FCSTD DOCUMENT  (FreeCAD 0.16R6706 (Git))
Label: femur
License: All rights reserved
LicenseURL: http://en.wikipedia.org/wiki/All_rights_reserved
objects: Sketcher::SketchObject×4
note: 4 computed .brp shape members not serialized (recipe doc carries the construction recipe); baked Part::Feature solids carry a one-line shape summary decoded from their .brp

FEATURE [Sketcher::SketchObject] Sketch003  label="femur_down"
  sketch-geometry (37):
    g0: LineSegment [constr] StartX=-7.72642 StartY=27.2442 StartZ=0 EndX=52.2736 EndY=27.2442 EndZ=0
    g1: GeomPoint [constr] X=-7.72642 Y=27.2442 Z=0
    g2: GeomPoint [constr] X=52.2736 Y=27.2442 Z=0
    g3: GeomPoint [constr] X=22.2736 Y=27.2442 Z=0
    g4: LineSegment [constr] StartX=22.2736 StartY=32.7442 StartZ=0 EndX=22.2736 EndY=21.7442 EndZ=0
    g5: LineSegment [constr] StartX=-7.72642 StartY=32.7442 StartZ=0 EndX=52.2736 EndY=32.7442 EndZ=0
    g6: LineSegment [constr] StartX=-7.72642 StartY=21.7442 StartZ=0 EndX=52.2736 EndY=21.7442 EndZ=0
    g7: Circle CenterX=52.2736 CenterY=27.2442 CenterZ=0 NormalX=0 NormalY=0 NormalZ=1 Radius=1.5
    g8: Circle CenterX=-7.72642 CenterY=27.2442 CenterZ=0 NormalX=0 NormalY=0 NormalZ=1 Radius=1.5
    g9: ArcOfCircle CenterX=52.2736 CenterY=27.2442 CenterZ=0 NormalX=0 NormalY=0 NormalZ=1 Radius=5.5 StartAngle=4.71239 EndAngle=7.85398
    g10: ArcOfCircle CenterX=-7.72642 CenterY=27.2442 CenterZ=0 NormalX=0 NormalY=0 NormalZ=1 Radius=5.5 StartAngle=1.5708 EndAngle=4.71239
    g11: LineSegment StartX=52.2736 StartY=32.7442 StartZ=0 EndX=32.0066 EndY=32.7442 EndZ=0
    g12: LineSegment [constr] StartX=29.0066 StartY=32.7442 StartZ=0 EndX=29.0066 EndY=24.7442 EndZ=0
    g13: LineSegment StartX=32.0066 StartY=21.7442 StartZ=0 EndX=32.0066 EndY=24.7442 EndZ=0
    g14: LineSegment StartX=29.0066 StartY=24.7442 StartZ=0 EndX=32.0066 EndY=24.7442 EndZ=0
    g15: LineSegment StartX=52.2736 StartY=21.7442 StartZ=0 EndX=32.0066 EndY=21.7442 EndZ=0
    g16: GeomPoint [constr] X=29.0066 Y=32.7442 Z=0
    g17: LineSegment StartX=29.0066 StartY=29.7442 StartZ=0 EndX=32.0066 EndY=29.7442 EndZ=0
    g18: LineSegment StartX=-7.72642 StartY=21.7442 StartZ=0 EndX=7.29856 EndY=21.7442 EndZ=0
    g19: LineSegment StartX=29.0066 StartY=24.7442 StartZ=0 EndX=29.0066 EndY=21.7442 EndZ=0
    g20: LineSegment [constr] StartX=18.6653 StartY=32.7442 StartZ=0 EndX=10.9612 EndY=21.7442 EndZ=0
    g21: LineSegment StartX=16.9443 StartY=30.287 StartZ=0 EndX=14.487 EndY=32.008 EndZ=0
    g22: LineSegment StartX=14.487 StartY=32.008 StartZ=0 EndX=15.0027 EndY=32.7442 EndZ=0
    g23: LineSegment StartX=-7.72642 StartY=32.7442 StartZ=0 EndX=15.0027 EndY=32.7442 EndZ=0
    g24: LineSegment StartX=10.9612 StartY=21.7442 StartZ=0 EndX=11.4768 EndY=22.4805 EndZ=0
    g25: LineSegment StartX=11.4768 StartY=22.4805 StartZ=0 EndX=9.01956 EndY=24.2015 EndZ=0
    g26: LineSegment StartX=9.01956 StartY=24.2015 StartZ=0 EndX=7.29856 EndY=21.7442 EndZ=0
    g27: LineSegment StartX=29.0066 StartY=21.7442 StartZ=0 EndX=10.9612 EndY=21.7442 EndZ=0
    g28: LineSegment StartX=29.0066 StartY=29.7442 StartZ=0 EndX=29.0066 EndY=32.7442 EndZ=0
    g29: LineSegment StartX=16.9443 StartY=30.287 StartZ=0 EndX=18.6653 EndY=32.7442 EndZ=0
    g30: LineSegment StartX=18.6653 StartY=32.7442 StartZ=0 EndX=29.0066 EndY=32.7442 EndZ=0
    g31: LineSegment [constr] StartX=29.0066 StartY=32.7442 StartZ=0 EndX=32.0066 EndY=32.7442 EndZ=0
    g32: LineSegment [constr] StartX=18.6653 StartY=32.7442 StartZ=0 EndX=16.208 EndY=34.4653 EndZ=0
    g33: LineSegment [constr] StartX=15.0027 StartY=32.7442 StartZ=0 EndX=16.208 EndY=34.4653 EndZ=0
    g34: Circle CenterX=21.7923 CenterY=27.2442 CenterZ=0 NormalX=0 NormalY=0 NormalZ=1 Radius=1.2
    g35: LineSegment [constr] StartX=22.9754 StartY=30.0156 StartZ=0 EndX=20.2417 EndY=23.6124 EndZ=0
    g36: LineSegment StartX=32.0066 StartY=32.7442 StartZ=0 EndX=32.0066 EndY=29.7442 EndZ=0
  constraints (96):
    c: PointOnObject(g1,g0)
    c: PointOnObject(g2,g0)
    c: Symmetric(g1,g2,g3)
    c: Distance(g3,g2) = 30
    c: Vertical(g4)
    c: Symmetric(g4,g4,g3)
    c: Distance(g3,g4) = 5.5
    c: Horizontal(g5)
    c: PointOnObject(g4,g5)
    c: Horizontal(g6)
    c: PointOnObject(g4,g6)
    c: Coincident(g7,g2)
    c: Radius(g7) = 1.5
    c: Coincident(g8,g1)
    c: Radius(g8) = 1.5
    c: Coincident(g9,g2)
    c: Coincident(g9,g6)
    c: Coincident(g5,g9)
    c: Tangent(g9,g5)
    c: Coincident(g10,g1)
    c: Coincident(g10,g6)
    c: Tangent(g6,g10)
    c: Coincident(g5,g10)
    c: Coincident(g11,g5)
    c: Coincident(g0,g2)
    c: Coincident(g0,g1)
    c: PointOnObject(g14,g12)
    c: Distance(g13,g13) = 3
    c: Coincident(g14,g13)
    c: Coincident(g15,g6)
    c: Perpendicular(g14,g12)
    c: Perpendicular(g14,g13)
    c: Distance(g13,g12) = 3
    c: PointOnObject(g17,g12)
    c: Distance(g17,g16) = 3
    c: Distance(g17,g17) = 3
    c: Perpendicular(g12,g17)
    c: PointOnObject(g12,g14)
    c: Coincident(g18,g6)
    c: PointOnObject(g13,g6)
    c: Coincident(g15,g13)
    c: Coincident(g19,g12)
    c: PointOnObject(g19,g6)
    c: Perpendicular(g14,g19)
    c: PointOnObject(g20,g6)
    c: PointOnObject(g21,g20)
    c: Distance(g21,g20) = 3
    c: Distance(g21,g21) = 3
    c: Perpendicular(g20,g21)
    c: Coincident(g22,g21)
    c: PointOnObject(g22,g5)
    c: Perpendicular(g21,g22)
    c: Coincident(g23,g5)
    c: Coincident(g22,g23)
    c: Coincident(g24,g20)
    c: PointOnObject(g24,g20)
    c: Coincident(g25,g24)
    c: Distance(g25,g24) = 3
    c: Coincident(g26,g25)
    c: PointOnObject(g26,g6)
    c: Distance(g26,g25) = 3
    c: Perpendicular(g25,g26)
    c: Perpendicular(g20,g25)
    c: Coincident(g18,g26)
    c: Coincident(g27,g19)
    c: Coincident(g20,g27)
    c: Coincident(g28,g12)
    c: Coincident(g17,g28)
    c: Coincident(g16,g12)
    c: PointOnObject(g12,g5)
    c: PointOnObject(g20,g5)
    c: Coincident(g29,g21)
    c: Coincident(g20,g29)
    c: Coincident(g30,g20)
    c: Coincident(g12,g30)
    c: Distance(g13,g0) = 21
    c: Tangent(g6,g9)
    c: Coincident(g31,g12)
    c: Perpendicular(g31,g12)
    c: Coincident(g32,g20)
    c: Perpendicular(g20,g32)
    c: Coincident(g33,g22)
    c: Parallel(g33,g22)
    c: Coincident(g32,g33)
    c: Distance(g18,g0) = 16
    c: Distance(g32,g0) = 25
    c: Radius(g34) = 1.2
    c: Symmetric(g24,g12,g35)
    c: Symmetric(g21,g17,g35)
    c: PointOnObject(g34,g35)
    c: PointOnObject(g34,g0)
    c: Coincident(g11,g31)
    c: Distance(g12,g11) = 3
    c: Coincident(g36,g11)
    c: Coincident(g17,g36)
    c: Horizontal(g11)
FEATURE [Sketcher::SketchObject] Sketch004  label="femur_up"
  sketch-geometry (51):
    g0: LineSegment [constr] StartX=-8.28939 StartY=9.55012 StartZ=0 EndX=51.7106 EndY=9.55012 EndZ=0
    g1: GeomPoint [constr] X=-8.28939 Y=9.55012 Z=0
    g2: GeomPoint [constr] X=51.7106 Y=9.55012 Z=0
    g3: GeomPoint [constr] X=21.7106 Y=9.55012 Z=0
    g4: LineSegment [constr] StartX=21.7106 StartY=15.0501 StartZ=0 EndX=21.7106 EndY=4.05012 EndZ=0
    g5: LineSegment [constr] StartX=-8.28939 StartY=15.0501 StartZ=0 EndX=51.7106 EndY=15.0501 EndZ=0
    g6: LineSegment [constr] StartX=-8.28939 StartY=4.05012 StartZ=0 EndX=51.7106 EndY=4.05012 EndZ=0
    g7: Circle CenterX=51.7106 CenterY=9.55012 CenterZ=0 NormalX=0 NormalY=0 NormalZ=1 Radius=3.5
    g8: Circle CenterX=-8.28939 CenterY=9.55012 CenterZ=0 NormalX=0 NormalY=0 NormalZ=1 Radius=3.5
    g9: LineSegment StartX=51.7106 StartY=15.0501 StartZ=0 EndX=31.4436 EndY=15.0501 EndZ=0
    g10: LineSegment [constr] StartX=28.4436 StartY=15.0501 StartZ=0 EndX=28.4436 EndY=7.05012 EndZ=0
    g11: LineSegment StartX=31.4436 StartY=4.05012 StartZ=0 EndX=31.4436 EndY=7.05012 EndZ=0
    g12: LineSegment StartX=28.4436 StartY=7.05012 StartZ=0 EndX=31.4436 EndY=7.05012 EndZ=0
    g13: LineSegment StartX=51.7106 StartY=4.05012 StartZ=0 EndX=31.4436 EndY=4.05012 EndZ=0
    g14: GeomPoint [constr] X=28.4436 Y=15.0501 Z=0
    g15: LineSegment StartX=28.4436 StartY=12.0501 StartZ=0 EndX=31.4436 EndY=12.0501 EndZ=0
    g16: LineSegment StartX=-8.28939 StartY=4.05012 StartZ=0 EndX=6.73559 EndY=4.05012 EndZ=0
    g17: LineSegment StartX=28.4436 StartY=7.05012 StartZ=0 EndX=28.4436 EndY=4.05012 EndZ=0
    g18: LineSegment [constr] StartX=18.1023 StartY=15.0501 StartZ=0 EndX=10.3982 EndY=4.05012 EndZ=0
    g19: LineSegment StartX=16.3813 StartY=12.5929 StartZ=0 EndX=13.924 EndY=14.3139 EndZ=0
    g20: LineSegment StartX=13.924 StartY=14.3139 StartZ=0 EndX=14.4397 EndY=15.0501 EndZ=0
    g21: LineSegment StartX=-8.28939 StartY=15.0501 StartZ=0 EndX=14.4397 EndY=15.0501 EndZ=0
    g22: LineSegment StartX=10.3982 StartY=4.05012 StartZ=0 EndX=10.9139 EndY=4.78638 EndZ=0
    g23: LineSegment StartX=10.9139 StartY=4.78638 StartZ=0 EndX=8.45659 EndY=6.50739 EndZ=0
    g24: LineSegment StartX=8.45659 StartY=6.50739 StartZ=0 EndX=6.73559 EndY=4.05012 EndZ=0
    g25: LineSegment StartX=28.4436 StartY=4.05012 StartZ=0 EndX=10.3982 EndY=4.05012 EndZ=0
    g26: LineSegment StartX=28.4436 StartY=12.0501 StartZ=0 EndX=28.4436 EndY=15.0501 EndZ=0
    g27: LineSegment StartX=16.3813 StartY=12.5929 StartZ=0 EndX=18.1023 EndY=15.0501 EndZ=0
    g28: LineSegment StartX=18.1023 StartY=15.0501 StartZ=0 EndX=28.4436 EndY=15.0501 EndZ=0
    g29: LineSegment [constr] StartX=28.4436 StartY=15.0501 StartZ=0 EndX=31.4436 EndY=15.0501 EndZ=0
    g30: LineSegment [constr] StartX=18.1023 StartY=15.0501 StartZ=0 EndX=15.645 EndY=16.7711 EndZ=0
    g31: LineSegment [constr] StartX=14.4397 StartY=15.0501 StartZ=0 EndX=15.645 EndY=16.7711 EndZ=0
    g32: Circle CenterX=21.2293 CenterY=9.55012 CenterZ=0 NormalX=0 NormalY=0 NormalZ=1 Radius=1.5
    g33: LineSegment [constr] StartX=22.4125 StartY=12.3215 StartZ=0 EndX=19.6787 EndY=5.91825 EndZ=0
    g34: LineSegment [constr] StartX=51.7106 StartY=15.0501 StartZ=0 EndX=51.7106 EndY=4.05012 EndZ=0
    g35: LineSegment [constr] StartX=-8.28939 StartY=15.0501 StartZ=0 EndX=-8.28939 EndY=4.05012 EndZ=0
    g36: Circle CenterX=45.2106 CenterY=9.55012 CenterZ=0 NormalX=0 NormalY=0 NormalZ=1 Radius=1.2
    g37: Circle CenterX=-1.78939 CenterY=9.55012 CenterZ=0 NormalX=0 NormalY=0 NormalZ=1 Radius=1.2
    g38: Circle CenterX=58.2106 CenterY=9.55012 CenterZ=0 NormalX=0 NormalY=0 NormalZ=1 Radius=1.2
    g39: Circle CenterX=-14.7894 CenterY=9.55012 CenterZ=0 NormalX=0 NormalY=0 NormalZ=1 Radius=1.2
    g40: ArcOfEllipse CenterX=51.7106 CenterY=9.55012 CenterZ=0 NormalX=0 NormalY=0 NormalZ=1 MajorRadius=10.5 MinorRadius=5.5 AngleXU=0 StartAngle=4.71239 EndAngle=7.85398
    g41: LineSegment [constr] StartX=62.2106 StartY=9.55012 StartZ=0 EndX=41.2106 EndY=9.55012 EndZ=0
    g42: LineSegment [constr] StartX=51.7106 StartY=15.0501 StartZ=0 EndX=51.7106 EndY=4.05012 EndZ=0
    g43: GeomPoint [constr] X=60.6549 Y=9.55012 Z=0
    g44: GeomPoint [constr] X=42.7663 Y=9.55012 Z=0
    g45: ArcOfEllipse CenterX=-8.28939 CenterY=9.55012 CenterZ=0 NormalX=0 NormalY=0 NormalZ=1 MajorRadius=10.5 MinorRadius=5.5 AngleXU=0 StartAngle=1.5708 EndAngle=4.71239
    g46: LineSegment [constr] StartX=2.21061 StartY=9.55012 StartZ=0 EndX=-18.7894 EndY=9.55012 EndZ=0
    g47: LineSegment [constr] StartX=-8.28939 StartY=15.0501 StartZ=0 EndX=-8.28939 EndY=4.05012 EndZ=0
    g48: GeomPoint [constr] X=0.654878 Y=9.55012 Z=0
    g49: GeomPoint [constr] X=-17.2337 Y=9.55012 Z=0
    g50: LineSegment StartX=31.4436 StartY=15.0501 StartZ=0 EndX=31.4436 EndY=12.0501 EndZ=0
  constraints (120):
    c: PointOnObject(g1,g0)
    c: PointOnObject(g2,g0)
    c: Symmetric(g1,g2,g3)
    c: Distance(g3,g2) = 30
    c: Vertical(g4)
    c: Symmetric(g4,g4,g3)
    c: Distance(g3,g4) = 5.5
    c: Horizontal(g5)
    c: PointOnObject(g4,g5)
    c: Horizontal(g6)
    c: PointOnObject(g4,g6)
    c: Coincident(g7,g2)
    c: Radius(g7) = 3.5
    c: Coincident(g8,g1)
    c: Radius(g8) = 3.5
    c: Coincident(g9,g5)
    c: Coincident(g0,g2)
    c: Coincident(g0,g1)
    c: PointOnObject(g12,g10)
    c: Distance(g11,g11) = 3
    c: Coincident(g12,g11)
    c: Coincident(g13,g6)
    c: Perpendicular(g12,g10)
    c: Perpendicular(g12,g11)
    c: Distance(g11,g10) = 3
    c: PointOnObject(g15,g10)
    c: Distance(g15,g14) = 3
    c: Distance(g15,g15) = 3
    c: Perpendicular(g10,g15)
    c: PointOnObject(g10,g12)
    c: Coincident(g16,g6)
    c: PointOnObject(g11,g6)
    c: Coincident(g13,g11)
    c: Coincident(g17,g10)
    c: PointOnObject(g17,g6)
    c: Perpendicular(g12,g17)
    c: PointOnObject(g18,g6)
    c: PointOnObject(g19,g18)
    c: Distance(g19,g18) = 3
    c: Distance(g19,g19) = 3
    c: Perpendicular(g18,g19)
    c: Coincident(g20,g19)
    c: PointOnObject(g20,g5)
    c: Perpendicular(g19,g20)
    c: Coincident(g21,g5)
    c: Coincident(g20,g21)
    c: Coincident(g22,g18)
    c: PointOnObject(g22,g18)
    c: Coincident(g23,g22)
    c: Distance(g23,g22) = 3
    c: Coincident(g24,g23)
    c: PointOnObject(g24,g6)
    c: Distance(g24,g23) = 3
    c: Perpendicular(g23,g24)
    c: Perpendicular(g18,g23)
    c: Coincident(g16,g24)
    c: Coincident(g25,g17)
    c: Coincident(g18,g25)
    c: Coincident(g26,g10)
    c: Coincident(g15,g26)
    c: Coincident(g14,g10)
    c: PointOnObject(g10,g5)
    c: PointOnObject(g18,g5)
    c: Coincident(g27,g19)
    c: Coincident(g18,g27)
    c: Coincident(g28,g18)
    c: Coincident(g10,g28)
    c: Distance(g11,g0) = 21
    c: Coincident(g29,g10)
    c: Perpendicular(g29,g10)
    c: Coincident(g30,g18)
    c: Perpendicular(g18,g30)
    c: Coincident(g31,g20)
    c: Parallel(g31,g20)
    c: Coincident(g30,g31)
    c: Distance(g16,g0) = 16
    c: Distance(g30,g0) = 25
    c: Radius(g32) = 1.5
    c: Symmetric(g22,g10,g33)
    c: Symmetric(g19,g15,g33)
    c: PointOnObject(g32,g33)
    c: Coincident(g34,g5)
    c: Coincident(g34,g6)
    c: Vertical(g34)
    c: Coincident(g35,g5)
    c: Coincident(g35,g6)
    c: Vertical(g35)
    c: PointOnObject(g0,g34)
    c: Distance(g0,g6) = 5.5
    c: PointOnObject(g0,g35)
    c: PointOnObject(g36,g0)
    c: Radius(g36) = 1.2
    c: Distance(g0,g36) = 6.5
    c: PointOnObject(g37,g0)
    c: Radius(g37) = 1.2
    c: Distance(g0,g37) = 6.5
    c: Radius(g38) = 1.2
    c: PointOnObject(g38,g0)
    c: Distance(g0,g38) = 6.5
    c: Radius(g39) = 1.2
    c: PointOnObject(g39,g0)
    c: Distance(g39,g0) = 6.5
    c: InternalAlignment(g41-g44 -> g40) x4
    c: Coincident(g40,g0)
    c: Coincident(g5,g42)
    c: PointOnObject(g40,g34)
    c: PointOnObject(g40,g34)
    c: InternalAlignment(g46-g49 -> g45) x4
    c: Coincident(g45,g0)
    c: Coincident(g6,g47)
    c: PointOnObject(g45,g35)
    c: PointOnObject(g45,g35)
    c: Distance(g38,g41) = 4
    c: Distance(g46,g39) = 4
    c: PointOnObject(g32,g0)
    c: Coincident(g9,g29)
    c: Coincident(g50,g9)
    c: Coincident(g50,g15)
    c: Perpendicular(g50,g15)
    c: Horizontal(g9)
FEATURE [Sketcher::SketchObject] Sketch005  label="femur_joint_tibia"
  sketch-geometry (16):
    g0: LineSegment [constr] StartX=4.47065 StartY=61.2395 StartZ=0 EndX=33.9706 EndY=61.2395 EndZ=0
    g1: LineSegment [constr] StartX=33.9706 StartY=61.2395 StartZ=0 EndX=33.9706 EndY=45.7095 EndZ=0
    g2: LineSegment [constr] StartX=33.9706 StartY=45.7095 StartZ=0 EndX=4.47065 EndY=45.7095 EndZ=0
    g3: LineSegment [constr] StartX=4.47065 StartY=45.7095 StartZ=0 EndX=4.47065 EndY=61.2395 EndZ=0
    g4: LineSegment StartX=1.47065 StartY=61.2395 StartZ=0 EndX=36.9706 EndY=61.2395 EndZ=0
    g5: LineSegment StartX=1.47065 StartY=45.7095 StartZ=0 EndX=36.9706 EndY=45.7095 EndZ=0
    g6: LineSegment StartX=36.9706 StartY=61.2395 StartZ=0 EndX=36.9706 EndY=58.2395 EndZ=0
    g7: LineSegment StartX=36.9706 StartY=45.7095 StartZ=0 EndX=36.9706 EndY=48.7095 EndZ=0
    g8: LineSegment StartX=36.9706 StartY=58.2395 StartZ=0 EndX=33.9706 EndY=58.2395 EndZ=0
    g9: LineSegment StartX=36.9706 StartY=48.7095 StartZ=0 EndX=33.9706 EndY=48.7095 EndZ=0
    g10: LineSegment StartX=33.9706 StartY=58.2395 StartZ=0 EndX=33.9706 EndY=48.7095 EndZ=0
    g11: LineSegment StartX=1.47065 StartY=61.2395 StartZ=0 EndX=1.47065 EndY=58.2395 EndZ=0
    g12: LineSegment StartX=1.47065 StartY=45.7095 StartZ=0 EndX=1.47065 EndY=48.7095 EndZ=0
    g13: LineSegment StartX=1.47065 StartY=48.7095 StartZ=0 EndX=4.47065 EndY=48.7095 EndZ=0
    g14: LineSegment StartX=1.47065 StartY=58.2395 StartZ=0 EndX=4.47065 EndY=58.2395 EndZ=0
    g15: LineSegment StartX=4.47065 StartY=58.2395 StartZ=0 EndX=4.47065 EndY=48.7095 EndZ=0
  constraints (46):
    c: Coincident(g0,g1)
    c: Coincident(g1,g2)
    c: Coincident(g2,g3)
    c: Coincident(g3,g0)
    c: Horizontal(g0)
    c: Horizontal(g2)
    c: Vertical(g1)
    c: Vertical(g3)
    c: Distance(g0,g3) = 29.5
    c: Distance(g1,g0) = 15.53
    c: PointOnObject(g0,g4)
    c: Distance(g4,g1) = 3
    c: Distance(g4,g3) = 3
    c: Horizontal(g5)
    c: PointOnObject(g1,g5)
    c: Horizontal(g4)
    c: Distance(g5,g3) = 3
    c: Distance(g5,g1) = 3
    c: Coincident(g6,g4)
    c: Coincident(g7,g5)
    c: Distance(g5,g7) = 3
    c: Distance(g6,g4) = 3
    c: Perpendicular(g5,g7)
    c: Perpendicular(g6,g4)
    c: Coincident(g8,g6)
    c: PointOnObject(g8,g1)
    c: Perpendicular(g1,g8)
    c: Coincident(g9,g7)
    c: PointOnObject(g9,g1)
    c: Perpendicular(g1,g9)
    c: Coincident(g10,g8)
    c: Coincident(g9,g10)
    c: Coincident(g11,g4)
    c: Coincident(g12,g5)
    c: Coincident(g13,g12)
    c: PointOnObject(g13,g3)
    c: PointOnObject(g14,g3)
    c: Distance(g14) = 3
    c: Coincident(g11,g14)
    c: Distance(g11,g4) = 3
    c: Distance(g12,g13) = 3
    c: Distance(g12,g5) = 3
    c: Perpendicular(g5,g12)
    c: Perpendicular(g4,g11)
    c: Coincident(g15,g14)
    c: Coincident(g13,g15)
FEATURE [Sketcher::SketchObject] Sketch006  label="femur_joint_coxa"
  sketch-geometry (16):
    g0: LineSegment [constr] StartX=5.11224 StartY=78.2192 StartZ=0 EndX=34.6122 EndY=78.2192 EndZ=0
    g1: LineSegment [constr] StartX=34.6122 StartY=78.2192 StartZ=0 EndX=34.6122 EndY=67.2192 EndZ=0
    g2: LineSegment [constr] StartX=34.6122 StartY=67.2192 StartZ=0 EndX=5.11224 EndY=67.2192 EndZ=0
    g3: LineSegment [constr] StartX=5.11224 StartY=67.2192 StartZ=0 EndX=5.11224 EndY=78.2192 EndZ=0
    g4: LineSegment StartX=2.11224 StartY=78.2192 StartZ=0 EndX=37.6122 EndY=78.2192 EndZ=0
    g5: LineSegment StartX=2.11224 StartY=67.2192 StartZ=0 EndX=37.6122 EndY=67.2192 EndZ=0
    g6: LineSegment StartX=37.6122 StartY=78.2192 StartZ=0 EndX=37.6122 EndY=75.2192 EndZ=0
    g7: LineSegment StartX=37.6122 StartY=67.2192 StartZ=0 EndX=37.6122 EndY=70.2192 EndZ=0
    g8: LineSegment StartX=37.6122 StartY=75.2192 StartZ=0 EndX=34.6122 EndY=75.2192 EndZ=0
    g9: LineSegment StartX=37.6122 StartY=70.2192 StartZ=0 EndX=34.6122 EndY=70.2192 EndZ=0
    g10: LineSegment StartX=34.6122 StartY=75.2192 StartZ=0 EndX=34.6122 EndY=70.2192 EndZ=0
    g11: LineSegment StartX=2.11224 StartY=78.2192 StartZ=0 EndX=2.11224 EndY=75.2192 EndZ=0
    g12: LineSegment StartX=2.11224 StartY=67.2192 StartZ=0 EndX=2.11224 EndY=70.2192 EndZ=0
    g13: LineSegment StartX=2.11224 StartY=70.2192 StartZ=0 EndX=5.11224 EndY=70.2192 EndZ=0
    g14: LineSegment StartX=2.11224 StartY=75.2192 StartZ=0 EndX=5.11224 EndY=75.2192 EndZ=0
    g15: LineSegment StartX=5.11224 StartY=75.2192 StartZ=0 EndX=5.11224 EndY=70.2192 EndZ=0
  constraints (46):
    c: Coincident(g0,g1)
    c: Coincident(g1,g2)
    c: Coincident(g2,g3)
    c: Coincident(g3,g0)
    c: Horizontal(g0)
    c: Horizontal(g2)
    c: Vertical(g1)
    c: Vertical(g3)
    c: Distance(g0,g3) = 29.5
    c: Distance(g1,g0) = 11
    c: PointOnObject(g0,g4)
    c: Distance(g4,g1) = 3
    c: Distance(g4,g3) = 3
    c: Horizontal(g5)
    c: PointOnObject(g1,g5)
    c: Horizontal(g4)
    c: Distance(g5,g3) = 3
    c: Distance(g5,g1) = 3
    c: Coincident(g6,g4)
    c: Coincident(g7,g5)
    c: Distance(g5,g7) = 3
    c: Distance(g6,g4) = 3
    c: Perpendicular(g5,g7)
    c: Perpendicular(g6,g4)
    c: Coincident(g8,g6)
    c: PointOnObject(g8,g1)
    c: Perpendicular(g1,g8)
    c: Coincident(g9,g7)
    c: PointOnObject(g9,g1)
    c: Perpendicular(g1,g9)
    c: Coincident(g10,g8)
    c: Coincident(g9,g10)
    c: Coincident(g11,g4)
    c: Coincident(g12,g5)
    c: Coincident(g13,g12)
    c: PointOnObject(g13,g3)
    c: PointOnObject(g14,g3)
    c: Distance(g14) = 3
    c: Coincident(g11,g14)
    c: Distance(g11,g4) = 3
    c: Distance(g12,g13) = 3
    c: Distance(g12,g5) = 3
    c: Perpendicular(g5,g12)
    c: Perpendicular(g4,g11)
    c: Coincident(g15,g14)
    c: Coincident(g13,g15)
